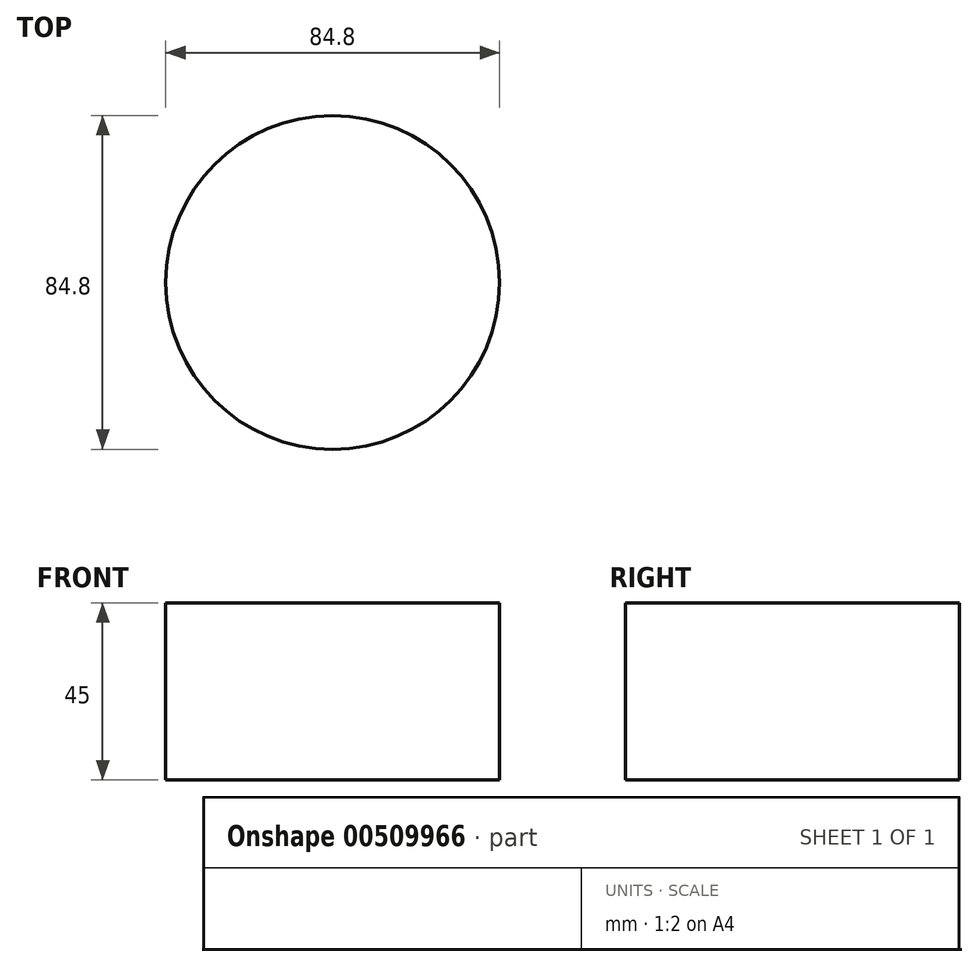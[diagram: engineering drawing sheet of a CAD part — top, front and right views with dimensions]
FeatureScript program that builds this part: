
annotation { "Feature Type Name" : "Feature", "Feature Type Description" : "" }
export const myFeature = defineFeature(function(context is Context, id is Id, definition is map)
    precondition{}
    {
        {
            var Q0;
            Q0=qCreatedBy(makeId("Top.planeOp"),FACE);
            var sketch = newSketch(context, id + "F0", { "sketchPlane" : qUnion([Q0])});
            skCircle(sketch, "E0", {"center": v(0, 0) * mm, "radius": 42.4 * mm});
            skSolve(sketch);
        }
        {
            var Q0;
            Q0 = qSketchRegion(id + "F0", true);
            extrude(context, id + "F1", {"entities" : qUnion([Q0]), "depth" : 45 * mm, "offsetDistance" : 25 * mm});
        }
    });
